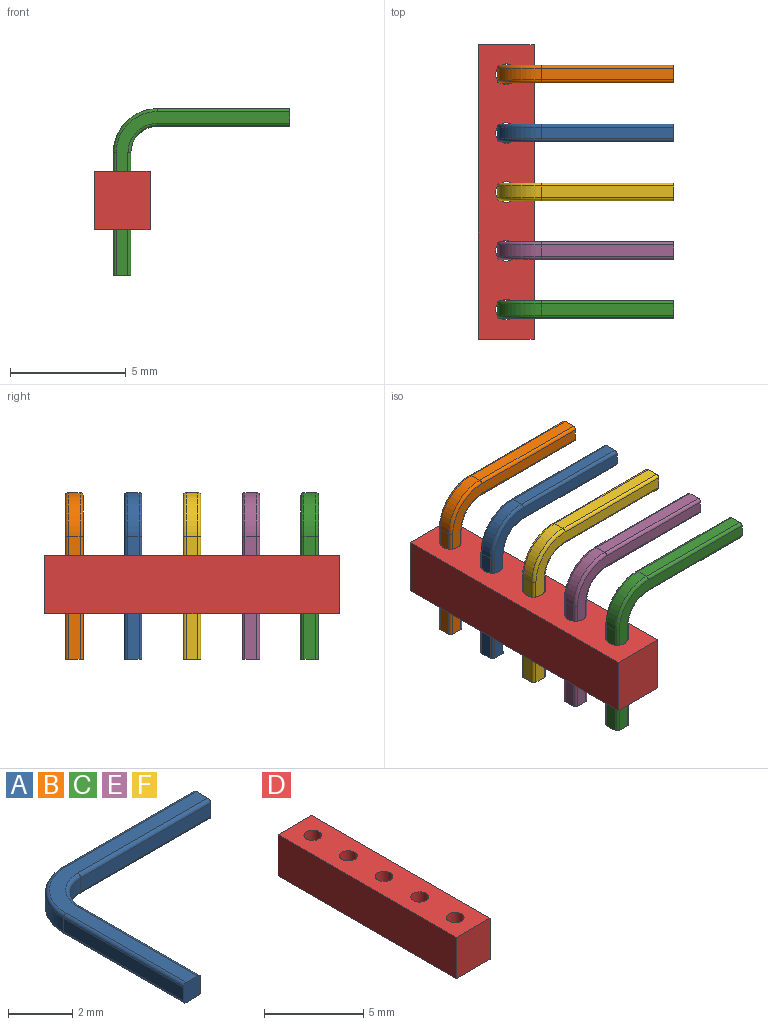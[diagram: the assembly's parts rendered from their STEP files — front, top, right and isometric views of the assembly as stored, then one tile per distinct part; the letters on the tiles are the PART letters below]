
ASSEMBLY  parts=6 mates=1
PART A: 22 faces, bbox 7.8x7.3x0.8 mm
  f0: torus R=1.78mm, axis (0,0,1), area 0.6mm2, adj f1,f4,f7,f8
  f1: cylinder r=0.13mm len=5.72mm, axis (-1,0,0), area 1.1mm2, adj f0,f3,f7,f10
  f2: cylinder r=0.13mm len=5.72mm, axis (1,0,0), area 1.1mm2, adj f5,f6,f7,f10
  f3: plane 5.72x0.51mm, normal (0,1,0), area 2.9mm2, adj f1,f4,f10,f11
  f4: cylinder r=1.91mm len=1.91mm, axis (0,0,1), area 1.5mm2, adj f0,f3,f9,f12
  f5: plane 5.72x0.51mm, normal (0,-1,0), area 2.9mm2, adj f2,f10,f14,f15
  f6: torus R=1.27mm, axis (0,0,-1), area 0.4mm2, adj f2,f7,f15,f16
  f7: plane 7.49x7.06mm, normal (0,0,1), area 6.8mm2, adj f0,f1,f2,f6,f8,f10,f16,f17
  f8: cylinder r=0.13mm len=5.28mm, axis (0,-1,0), area 1.1mm2, adj f0,f7,f9,f17
  f9: plane 5.28x0.51mm, normal (-1,0,0), area 2.7mm2, adj f4,f8,f13,f17
  f10: plane 0.76x0.76mm, normal (1,0,0), area 0.6mm2, adj f1,f2,f3,f5,f7,f11,f14,f18
  f11: cylinder r=0.13mm len=5.72mm, axis (-1,0,0), area 1.1mm2, adj f3,f10,f12,f18
  f12: torus R=1.78mm, axis (0,0,1), area 0.6mm2, adj f4,f11,f13,f18
  f13: cylinder r=0.13mm len=5.28mm, axis (0,-1,0), area 1.1mm2, adj f9,f12,f17,f18
  f14: cylinder r=0.13mm len=5.72mm, axis (1,0,0), area 1.1mm2, adj f5,f10,f18,f19
  f15: cylinder r=1.14mm len=1.14mm, axis (0,0,1), area 0.9mm2, adj f5,f6,f19,f20
  f16: cylinder r=0.13mm len=5.28mm, axis (0,1,0), area 1.1mm2, adj f6,f7,f17,f20
  f17: plane 0.76x0.76mm, normal (0,-1,0), area 0.6mm2, adj f7,f8,f9,f13,f16,f18,f20,f21
  f18: plane 7.49x7.06mm, normal (0,0,-1), area 6.8mm2, adj f10,f11,f12,f13,f14,f17,f19,f21
  f19: torus R=1.27mm, axis (0,0,-1), area 0.4mm2, adj f14,f15,f18,f21
  f20: plane 5.28x0.51mm, normal (1,0,0), area 2.7mm2, adj f15,f16,f17,f21
  f21: cylinder r=0.13mm len=5.28mm, axis (0,1,0), area 1.1mm2, adj f17,f18,f19,f20
PART B: same geometry as A
PART C: same geometry as A
PART D: 11 faces, bbox 2.4x12.7x2.5 mm
  f0: cylinder r=0.44mm len=2.54mm, axis (0,0,1), area 7.1mm2, adj f8,f9
  f1: cylinder r=0.44mm len=2.54mm, axis (0,0,1), area 7.1mm2, adj f8,f9
  f2: cylinder r=0.44mm len=2.54mm, axis (0,0,1), area 7.1mm2, adj f8,f9
  f3: cylinder r=0.44mm len=2.54mm, axis (0,0,1), area 7.1mm2, adj f8,f9
  f4: plane 2.54x2.41mm, normal (0,-1,0), area 6.1mm2, adj f5,f7,f8,f9
  f5: plane 12.7x2.54mm, normal (1,0,0), area 32.3mm2, adj f4,f6,f8,f9
  f6: plane 2.54x2.41mm, normal (0,1,0), area 6.1mm2, adj f5,f7,f8,f9
  f7: plane 12.7x2.54mm, normal (-1,0,0), area 32.3mm2, adj f4,f6,f8,f9
  f8: plane 12.7x2.41mm, normal (0,0,-1), area 27.5mm2, adj f0,f1,f2,f3,f4,f5,f6,f7
  f9: plane 12.7x2.41mm, normal (0,0,1), area 27.5mm2, adj f0,f1,f2,f3,f4,f5,f6,f7
  f10: cylinder r=0.44mm len=2.54mm, axis (0,0,1), area 7.1mm2, adj f8,f9
PART E: same geometry as A
PART F: same geometry as A
PLACE A rot(axis=(1,0,0),90deg) t=(-0.85,5.74,6.18)mm
PLACE B rot(axis=(1,0,0),90deg) t=(-0.85,8.28,6.18)mm
PLACE C rot(axis=(1,0,0),90deg) t=(-0.85,-1.88,6.18)mm
PLACE D t=(-1.67,-3.53,3.37)mm
PLACE E rot(axis=(1,0,0),90deg) t=(-0.85,0.66,6.18)mm
PLACE F rot(axis=(1,0,0),90deg) t=(-0.85,3.2,6.18)mm
MATE fastened C.f17 <-> D.f10  axis (0,0,-1) through (-0.47,-2.26,1.41)mm
